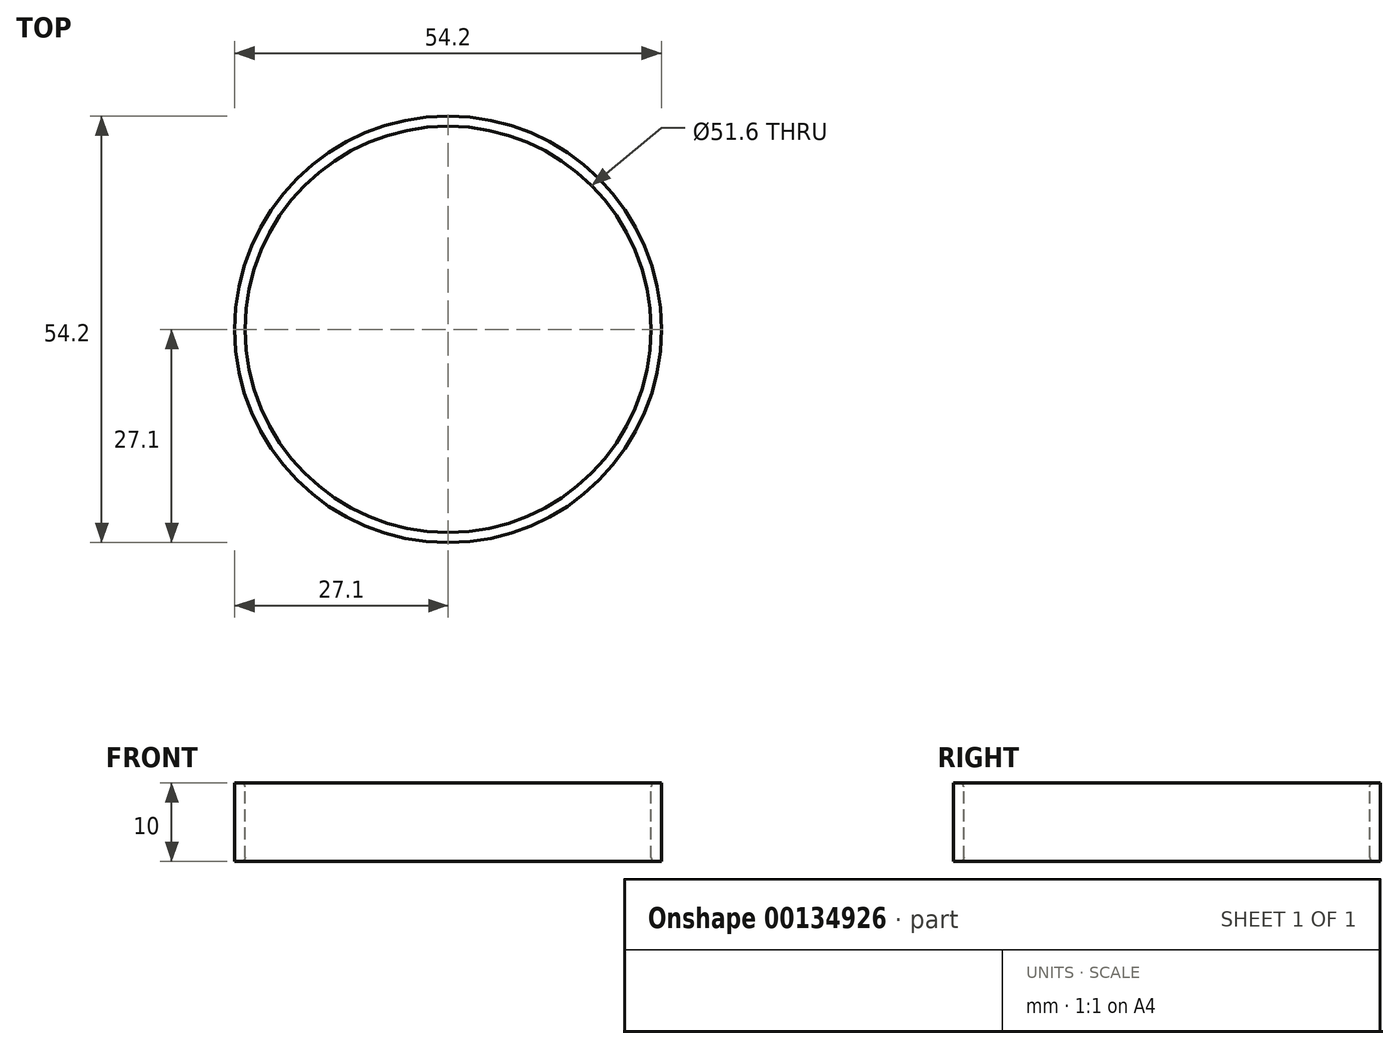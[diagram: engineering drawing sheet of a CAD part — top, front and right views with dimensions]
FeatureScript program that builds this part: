
annotation { "Feature Type Name" : "Feature", "Feature Type Description" : "" }
export const myFeature = defineFeature(function(context is Context, id is Id, definition is map)
    precondition{}
    {
        {
            var Q0;
            Q0=qCreatedBy(makeId("Top.planeOp"),FACE);
            var sketch = newSketch(context, id + "F0", { "sketchPlane" : qUnion([Q0])});
            skCircle(sketch, "E0", {"center": v(0, 0) * mm, "radius": 27.1 * mm});
            skCircle(sketch, "E1", {"center": v(0, 0) * mm, "radius": 25.8 * mm});
            skSolve(sketch);
        }
        {
            var Q0;
            Q0=makeQuery(id+"F0.imprint","IMPRINT",FACE,{"disambiguationData":[TD([[makeQuery(id+"F0.imprint","IMPRINT",EDGE,{"derivedFrom":sQuery(id+"F0.wireOp",EDGE,"E0")}),1.0]])]});
            var Q1;
            Q1=makeQuery(id+"F0.imprint","IMPRINT",FACE,{"disambiguationData":[TD([[makeQuery(id+"F0.imprint","IMPRINT",EDGE,{"derivedFrom":sQuery(id+"F0.wireOp",EDGE,"E0")}),-1.0]])]});
            var Q2;
            Q2=makeQuery(id+"F0.imprint","IMPRINT",FACE,{"disambiguationData":[TD([[makeQuery(id+"F0.imprint","IMPRINT",EDGE,{"derivedFrom":sQuery(id+"F0.wireOp",EDGE,"VDpK7lxK-j2Hn-RRng-n2O2-9wenkiVkwFwV")}),1.0]])]});
            extrude(context, id + "F1", {"entities" : qUnion([Q0, Q1, Q2]), "oppositeDirection" : true, "depth" : 10 * mm});
        }
        {
            var Q0;
            Q0=makeQuery(id+"F1.opExtrude","CAP_EDGE",EDGE,{"disambiguationData":[OSD([sQuery(id+"F0.wireOp",EDGE,"E1")])],"isStart":true});
            var Q1;
            Q1=makeQuery(id+"F1.opExtrude","CAP_EDGE",EDGE,{"disambiguationData":[OSD([sQuery(id+"F0.wireOp",EDGE,"E1")])],"isStart":false});
            fillet(context, id + "F2", {"entities" : qUnion([Q0, Q1]), "radius" : 0.5 * mm, "tangentPropagation" : true, "allowEdgeOverflow" : false});
        }
    });
